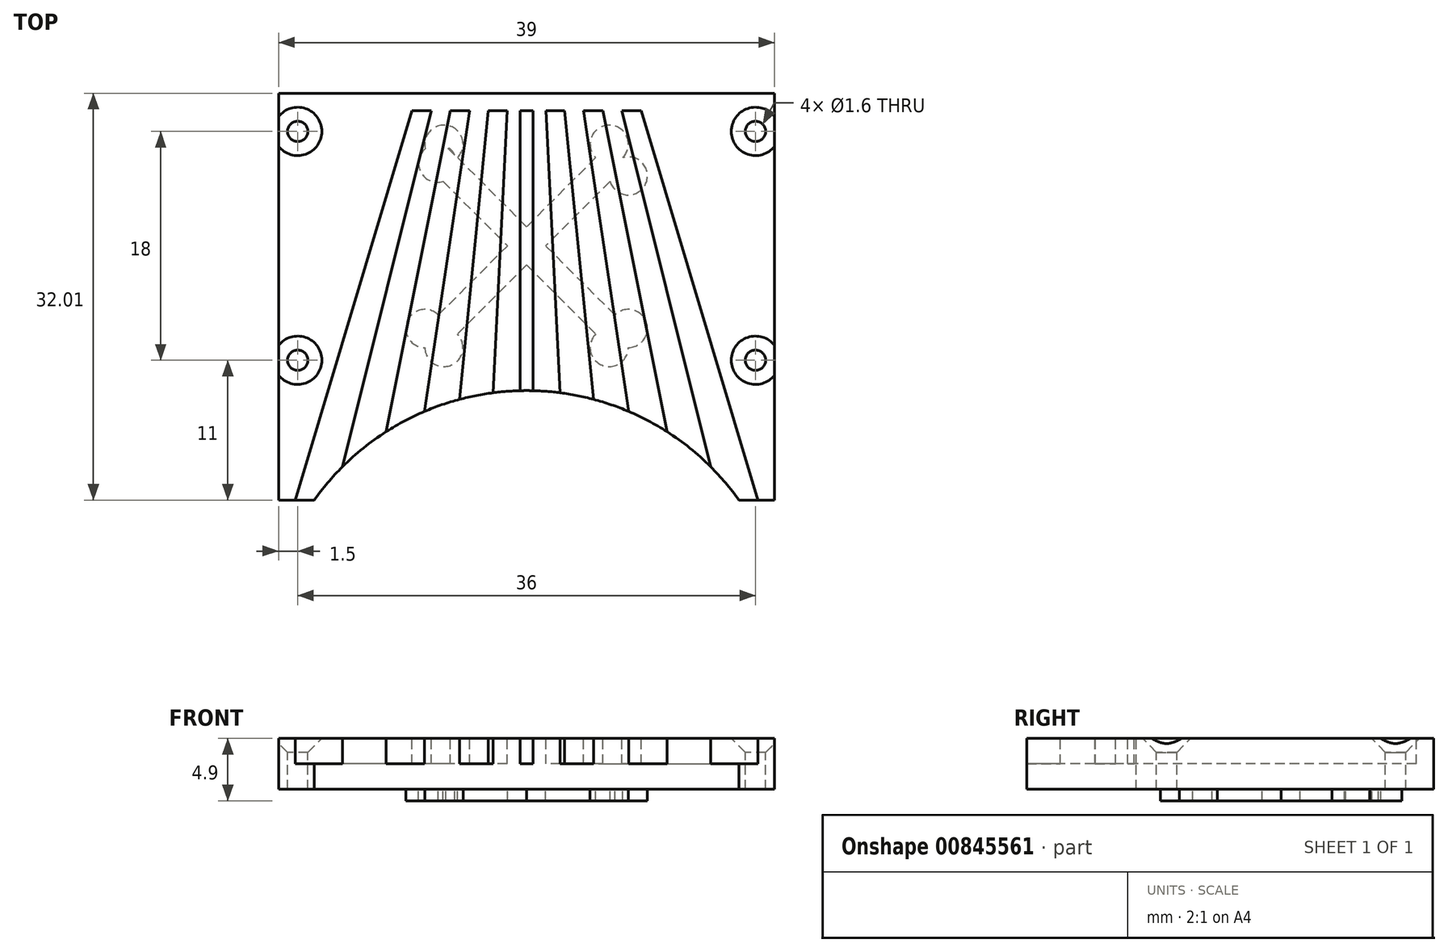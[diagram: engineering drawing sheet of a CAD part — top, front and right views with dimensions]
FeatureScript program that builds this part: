
annotation { "Feature Type Name" : "Feature", "Feature Type Description" : "" }
export const myFeature = defineFeature(function(context is Context, id is Id, definition is map)
    precondition{}
    {
        {
            var Q0;
            Q0=qCreatedBy(makeId("Top.planeOp"),FACE);
            var sketch = newSketch(context, id + "F0", { "sketchPlane" : qUnion([Q0])});
            skLineSegment(sketch, "E0.bottom", {"start": v(19.5, -20) * mm, "end": v(-19.5, -20) * mm});
            skLineSegment(sketch, "E0.top", {"start": v(19.5, 20) * mm, "end": v(-19.5, 20) * mm});
            skLineSegment(sketch, "E0.left", {"start": v(19.5, -20) * mm, "end": v(19.5, 20) * mm});
            skLineSegment(sketch, "E0.right", {"start": v(-19.5, -20) * mm, "end": v(-19.5, 20) * mm});
            skPoint(sketch, "E0.middle", {"position": v(0, 0) * mm});
            skSolve(sketch);
        }
        {
            var Q0;
            Q0=makeQuery(id+"F0.imprint","IMPRINT",FACE,{"disambiguationData":[TD([[makeQuery(id+"F0.imprint","IMPRINT",EDGE,{"derivedFrom":sQuery(id+"F0.wireOp",EDGE,"E0.bottom")}),-1.0]])]});
            extrude(context, id + "F1", {"entities" : qUnion([Q0]), "depth" : 4 * mm});
        }
        {
            var Q0;
            Q0=makeQuery(id+"F1.opExtrude","CAP_FACE",FACE,{"disambiguationData":[OSD([sQuery(id+"F0.wireOp",EDGE,"E0.bottom"),sQuery(id+"F0.wireOp",EDGE,"E0.top"),sQuery(id+"F0.wireOp",EDGE,"E0.left"),sQuery(id+"F0.wireOp",EDGE,"E0.right")])],"isStart":true});
            var sketch = newSketch(context, id + "F2", { "sketchPlane" : qUnion([Q0])});
            skLineSegment(sketch, "E1.bottom", {"start": v(-20.5, 20) * mm, "end": v(20.5, 20) * mm});
            skLineSegment(sketch, "E1.top", {"start": v(-20.5, -12) * mm, "end": v(20.5, -12) * mm});
            skLineSegment(sketch, "E1.left", {"start": v(-20.5, 20) * mm, "end": v(-20.5, -12) * mm});
            skLineSegment(sketch, "E1.right", {"start": v(20.5, 20) * mm, "end": v(20.5, -12) * mm});
            skSolve(sketch);
        }
        {
            var Q0;
            Q0=makeQuery(id+"F1.opExtrude","CAP_FACE",FACE,{"disambiguationData":[OSD([sQuery(id+"F0.wireOp",EDGE,"E0.bottom"),sQuery(id+"F0.wireOp",EDGE,"E0.top"),sQuery(id+"F0.wireOp",EDGE,"E0.left"),sQuery(id+"F0.wireOp",EDGE,"E0.right")])],"isStart":false});
            var sketch = newSketch(context, id + "F3", { "sketchPlane" : qUnion([Q0])});
            skLineSegment(sketch, "E2.left", {"start": v(-20.5, -20) * mm, "end": v(-20.5, 5) * mm});
            skCircle(sketch, "E3", {"center": v(0, -31.89) * mm, "radius": 20.5 * mm});
            skLineSegment(sketch, "E4.left", {"start": v(20.5, -20) * mm, "end": v(20.5, 5) * mm});
            skSolve(sketch);
        }
        {
            var Q0;
            Q0=makeQuery(id+"F3.imprint","IMPRINT",FACE,{"disambiguationData":[TD([[makeQuery(id+"F3.imprint","IMPRINT",EDGE,{"derivedFrom":sQuery(id+"F3.wireOp",EDGE,"E3")}),1.0]])]});
            extrude(context, id + "F4", {"entities" : qUnion([Q0]), "operationType" : NewBodyOperationType.REMOVE, "oppositeDirection" : true, "depth" : 25 * mm});
        }
        {
            var Q0;
            Q0=makeQuery(id+"F1.opExtrude","CAP_FACE",FACE,{"disambiguationData":[OSD([sQuery(id+"F0.wireOp",EDGE,"E0.bottom"),sQuery(id+"F0.wireOp",EDGE,"E0.top"),sQuery(id+"F0.wireOp",EDGE,"E0.left"),sQuery(id+"F0.wireOp",EDGE,"E0.right")])],"isStart":false});
            var sketch = newSketch(context, id + "F5", { "sketchPlane" : qUnion([Q0])});
            skLineSegment(sketch, "E5.bottom", {"start": v(19.5, 20) * mm, "end": v(-19.5, 20) * mm});
            skLineSegment(sketch, "E5.top", {"start": v(19.5, 12) * mm, "end": v(-19.5, 12) * mm});
            skLineSegment(sketch, "E5.left", {"start": v(19.5, 20) * mm, "end": v(19.5, 12) * mm});
            skLineSegment(sketch, "E5.right", {"start": v(-19.5, 20) * mm, "end": v(-19.5, 12) * mm});
            skSolve(sketch);
        }
        {
            var Q0;
            Q0=makeQuery(id+"F5.imprint","IMPRINT",FACE,{"disambiguationData":[TD([[makeQuery(id+"F5.imprint","IMPRINT",EDGE,{"derivedFrom":sQuery(id+"F5.wireOp",EDGE,"E5.bottom")}),1.0]])]});
            extrude(context, id + "F6", {"entities" : qUnion([Q0]), "operationType" : NewBodyOperationType.REMOVE, "oppositeDirection" : true, "depth" : 25 * mm});
        }
        {
            var Q0;
            Q0=makeQuery(id+"F1.opExtrude","CAP_FACE",FACE,{"disambiguationData":[OSD([sQuery(id+"F0.wireOp",EDGE,"E0.bottom"),sQuery(id+"F0.wireOp",EDGE,"E0.top"),sQuery(id+"F0.wireOp",EDGE,"E0.left"),sQuery(id+"F0.wireOp",EDGE,"E0.right")])],"isStart":false});
            var sketch = newSketch(context, id + "F7", { "sketchPlane" : qUnion([Q0])});
            skCircle(sketch, "E6", {"center": v(0, 40.68) * mm, "radius": 20.5 * mm});
            skLineSegment(sketch, "E7", {"start": v(0, 40.68) * mm, "end": v(0, -11.39) * mm, "construction": true});
            skLineSegment(sketch, "E8", {"start": v(0, 40.68) * mm, "end": v(2.51, -8.88) * mm, "construction": true});
            skLineSegment(sketch, "E9", {"start": v(0, 40.68) * mm, "end": v(5.03, -9.7) * mm, "construction": true});
            skLineSegment(sketch, "E10.bottom", {"start": v(-0.5, 10.63) * mm, "end": v(0.5, 10.63) * mm});
            skLineSegment(sketch, "E10.top", {"start": v(-0.5, -16.72) * mm, "end": v(0.5, -16.72) * mm});
            skLineSegment(sketch, "E10.left", {"start": v(-0.5, 10.63) * mm, "end": v(-0.5, -16.72) * mm});
            skLineSegment(sketch, "E10.right", {"start": v(0.5, 10.63) * mm, "end": v(0.5, -16.72) * mm});
            skPoint(sketch, "E10.middle", {"position": v(0, -3.05) * mm});
            skLineSegment(sketch, "E11", {"start": v(0, 40.68) * mm, "end": v(7.5, -9.48) * mm, "construction": true});
            skLineSegment(sketch, "E12", {"start": v(0, 40.68) * mm, "end": v(10.03, -9.53) * mm, "construction": true});
            skLineSegment(sketch, "E13", {"start": v(0, 40.68) * mm, "end": v(12.45, -9.27) * mm, "construction": true});
            skLineSegment(sketch, "E14", {"start": v(0, 40.68) * mm, "end": v(15, -9.32) * mm, "construction": true});
            skLineSegment(sketch, "E15", {"start": v(0, 40.68) * mm, "end": v(-2.53, -9.2) * mm, "construction": true});
            skLineSegment(sketch, "E16", {"start": v(0, 40.68) * mm, "end": v(-4.93, -8.73) * mm, "construction": true});
            skLineSegment(sketch, "E17", {"start": v(0, 40.68) * mm, "end": v(-7.45, -9.16) * mm, "construction": true});
            skLineSegment(sketch, "E18", {"start": v(0, 40.68) * mm, "end": v(-10.25, -10.6) * mm, "construction": true});
            skLineSegment(sketch, "E19", {"start": v(0, 40.68) * mm, "end": v(-12.9, -11.1) * mm, "construction": true});
            skLineSegment(sketch, "E20", {"start": v(0, 40.68) * mm, "end": v(-15.32, -10.37) * mm, "construction": true});
            skLineSegment(sketch, "E21", {"start": v(-0.5, 10.63) * mm, "end": v(-19.5, 10.63) * mm, "construction": true});
            skLineSegment(sketch, "E22", {"start": v(0.5, 10.63) * mm, "end": v(19.5, 10.63) * mm, "construction": true});
            skLineSegment(sketch, "E23", {"start": v(9.02, 10.63) * mm, "end": v(9.52, 10.63) * mm});
            skLineSegment(sketch, "E24", {"start": v(9.02, 10.63) * mm, "end": v(8.52, 10.63) * mm});
            skLineSegment(sketch, "E25", {"start": v(7.5, 10.63) * mm, "end": v(8, 10.63) * mm});
            skLineSegment(sketch, "E26", {"start": v(7.5, 10.63) * mm, "end": v(7, 10.63) * mm});
            skLineSegment(sketch, "E27", {"start": v(6, 10.63) * mm, "end": v(6.5, 10.63) * mm});
            skLineSegment(sketch, "E28", {"start": v(6, 10.63) * mm, "end": v(5.5, 10.63) * mm});
            skLineSegment(sketch, "E29", {"start": v(4.5, 10.63) * mm, "end": v(5, 10.63) * mm});
            skLineSegment(sketch, "E30", {"start": v(4.5, 10.63) * mm, "end": v(3.99, 10.63) * mm});
            skLineSegment(sketch, "E31", {"start": v(3, 10.63) * mm, "end": v(3.5, 10.63) * mm});
            skLineSegment(sketch, "E32", {"start": v(3, 10.63) * mm, "end": v(2.5, 10.63) * mm});
            skLineSegment(sketch, "E33", {"start": v(1.52, 10.63) * mm, "end": v(2.03, 10.63) * mm});
            skLineSegment(sketch, "E34", {"start": v(1.52, 10.63) * mm, "end": v(1.02, 10.63) * mm});
            skLineSegment(sketch, "E35", {"start": v(-1.52, 10.63) * mm, "end": v(-1.02, 10.63) * mm});
            skLineSegment(sketch, "E36", {"start": v(-1.52, 10.63) * mm, "end": v(-2.02, 10.63) * mm});
            skLineSegment(sketch, "E37", {"start": v(-3, 10.63) * mm, "end": v(-2.5, 10.63) * mm});
            skLineSegment(sketch, "E38", {"start": v(-3, 10.63) * mm, "end": v(-3.5, 10.63) * mm});
            skLineSegment(sketch, "E39", {"start": v(-4.5, 10.63) * mm, "end": v(-3.98, 10.63) * mm});
            skLineSegment(sketch, "E40", {"start": v(-4.5, 10.63) * mm, "end": v(-5, 10.63) * mm});
            skLineSegment(sketch, "E41", {"start": v(-6, 10.63) * mm, "end": v(-5.5, 10.63) * mm});
            skLineSegment(sketch, "E42", {"start": v(-6, 10.63) * mm, "end": v(-6.5, 10.63) * mm});
            skLineSegment(sketch, "E43", {"start": v(-7.5, 10.63) * mm, "end": v(-7, 10.63) * mm});
            skLineSegment(sketch, "E44", {"start": v(-7.5, 10.63) * mm, "end": v(-8, 10.63) * mm});
            skLineSegment(sketch, "E45", {"start": v(-9.02, 10.63) * mm, "end": v(-8.5, 10.63) * mm});
            skLineSegment(sketch, "E46", {"start": v(-9.02, 10.63) * mm, "end": v(-9.52, 10.63) * mm});
            skLineSegment(sketch, "E47", {"start": v(19.5, -20) * mm, "end": v(-19.5, -20) * mm, "construction": true});
            skLineSegment(sketch, "E48", {"start": v(18.2, -20) * mm, "end": v(18.7, -20) * mm});
            skLineSegment(sketch, "E49", {"start": v(18.2, -20) * mm, "end": v(17.7, -20) * mm});
            skLineSegment(sketch, "E50", {"start": v(15.13, -20) * mm, "end": v(15.63, -20) * mm});
            skLineSegment(sketch, "E51", {"start": v(15.13, -20) * mm, "end": v(14.63, -20) * mm});
            skLineSegment(sketch, "E52", {"start": v(12.12, -20) * mm, "end": v(12.63, -20) * mm});
            skLineSegment(sketch, "E53", {"start": v(12.12, -20) * mm, "end": v(11.62, -20) * mm});
            skLineSegment(sketch, "E54", {"start": v(9.07, -20) * mm, "end": v(9.57, -20) * mm});
            skLineSegment(sketch, "E55", {"start": v(9.07, -20) * mm, "end": v(8.57, -20) * mm});
            skLineSegment(sketch, "E56", {"start": v(6.06, -20) * mm, "end": v(6.56, -20) * mm});
            skLineSegment(sketch, "E57", {"start": v(6.06, -20) * mm, "end": v(5.56, -20) * mm});
            skLineSegment(sketch, "E58", {"start": v(3.08, -20) * mm, "end": v(3.58, -20) * mm});
            skLineSegment(sketch, "E59", {"start": v(3.08, -20) * mm, "end": v(2.57, -20) * mm});
            skLineSegment(sketch, "E60", {"start": v(-3.07, -20) * mm, "end": v(-2.57, -20) * mm});
            skLineSegment(sketch, "E61", {"start": v(-3.07, -20) * mm, "end": v(-3.57, -20) * mm});
            skLineSegment(sketch, "E62", {"start": v(-6.06, -20) * mm, "end": v(-5.55, -20) * mm});
            skLineSegment(sketch, "E63", {"start": v(-6.06, -20) * mm, "end": v(-6.56, -20) * mm});
            skLineSegment(sketch, "E64", {"start": v(-9.06, -20) * mm, "end": v(-8.56, -20) * mm});
            skLineSegment(sketch, "E65", {"start": v(-9.06, -20) * mm, "end": v(-9.56, -20) * mm});
            skLineSegment(sketch, "E66", {"start": v(-12.12, -20) * mm, "end": v(-11.62, -20) * mm});
            skLineSegment(sketch, "E67", {"start": v(-12.12, -20) * mm, "end": v(-12.63, -20) * mm});
            skLineSegment(sketch, "E68", {"start": v(-15.13, -20) * mm, "end": v(-14.63, -20) * mm});
            skLineSegment(sketch, "E69", {"start": v(-15.13, -20) * mm, "end": v(-15.63, -20) * mm});
            skLineSegment(sketch, "E70", {"start": v(-18.2, -20) * mm, "end": v(-17.7, -20) * mm});
            skLineSegment(sketch, "E71", {"start": v(-18.2, -20) * mm, "end": v(-18.7, -20) * mm});
            skLineSegment(sketch, "E72", {"start": v(1.52, 10.63) * mm, "end": v(3.08, -20) * mm});
            skLineSegment(sketch, "E73", {"start": v(3, 10.63) * mm, "end": v(6.06, -20) * mm});
            skLineSegment(sketch, "E74", {"start": v(4.5, 10.63) * mm, "end": v(9.07, -20) * mm});
            skLineSegment(sketch, "E75", {"start": v(6, 10.63) * mm, "end": v(12.12, -20) * mm});
            skLineSegment(sketch, "E76", {"start": v(7.5, 10.63) * mm, "end": v(15.13, -20) * mm});
            skLineSegment(sketch, "E77", {"start": v(9.02, 10.63) * mm, "end": v(18.2, -20) * mm});
            skLineSegment(sketch, "E78", {"start": v(9.02, 10.63) * mm, "end": v(7.5, 10.63) * mm});
            skLineSegment(sketch, "E79", {"start": v(6, 10.63) * mm, "end": v(4.5, 10.63) * mm});
            skLineSegment(sketch, "E80", {"start": v(3, 10.63) * mm, "end": v(1.52, 10.63) * mm});
            skLineSegment(sketch, "E81", {"start": v(18.2, -20) * mm, "end": v(15.13, -20) * mm});
            skLineSegment(sketch, "E82", {"start": v(12.12, -20) * mm, "end": v(9.07, -20) * mm});
            skLineSegment(sketch, "E83", {"start": v(6.06, -20) * mm, "end": v(3.08, -20) * mm});
            skLineSegment(sketch, "E84", {"start": v(-1.52, 10.63) * mm, "end": v(-3.07, -20) * mm});
            skLineSegment(sketch, "E85", {"start": v(-3, 10.63) * mm, "end": v(-6.06, -20) * mm});
            skLineSegment(sketch, "E86", {"start": v(-4.5, 10.63) * mm, "end": v(-9.06, -20) * mm});
            skLineSegment(sketch, "E87", {"start": v(-6, 10.63) * mm, "end": v(-12.12, -20) * mm});
            skLineSegment(sketch, "E88", {"start": v(-7.5, 10.63) * mm, "end": v(-15.13, -20) * mm});
            skLineSegment(sketch, "E89", {"start": v(-9.02, 10.63) * mm, "end": v(-18.2, -20) * mm});
            skLineSegment(sketch, "E90", {"start": v(-1.52, 10.63) * mm, "end": v(-3, 10.63) * mm});
            skLineSegment(sketch, "E91", {"start": v(-4.5, 10.63) * mm, "end": v(-6, 10.63) * mm});
            skLineSegment(sketch, "E92", {"start": v(-7.5, 10.63) * mm, "end": v(-9.02, 10.63) * mm});
            skLineSegment(sketch, "E93", {"start": v(-3.07, -20) * mm, "end": v(-6.06, -20) * mm});
            skLineSegment(sketch, "E94", {"start": v(-9.06, -20) * mm, "end": v(-12.12, -20) * mm});
            skLineSegment(sketch, "E95", {"start": v(-15.13, -20) * mm, "end": v(-18.2, -20) * mm});
            skSolve(sketch);
        }
        {
            var Q0;
            Q0=makeQuery(id+"F1.opExtrude","CAP_FACE",FACE,{"disambiguationData":[OSD([sQuery(id+"F0.wireOp",EDGE,"E0.bottom"),sQuery(id+"F0.wireOp",EDGE,"E0.top"),sQuery(id+"F0.wireOp",EDGE,"E0.left"),sQuery(id+"F0.wireOp",EDGE,"E0.right")])],"isStart":false});
            var sketch = newSketch(context, id + "F8", { "sketchPlane" : qUnion([Q0])});
            skLineSegment(sketch, "E96.bottom", {"start": v(-18, -9) * mm, "end": v(18, -9) * mm, "construction": true});
            skLineSegment(sketch, "E96.top", {"start": v(-18, 9) * mm, "end": v(18, 9) * mm, "construction": true});
            skLineSegment(sketch, "E96.left", {"start": v(-18, -9) * mm, "end": v(-18, 9) * mm, "construction": true});
            skLineSegment(sketch, "E96.right", {"start": v(18, -9) * mm, "end": v(18, 9) * mm, "construction": true});
            skPoint(sketch, "E96.middle", {"position": v(0, 0) * mm});
            skCircle(sketch, "E97", {"center": v(18, 9) * mm, "radius": 0.8 * mm});
            skCircle(sketch, "E98", {"center": v(18, -9) * mm, "radius": 0.8 * mm});
            skCircle(sketch, "E99", {"center": v(-18, 9) * mm, "radius": 0.8 * mm});
            skCircle(sketch, "E100", {"center": v(-18, -9) * mm, "radius": 0.8 * mm});
            skSolve(sketch);
        }
        {
            var Q0;
            Q0=sQuery(id+"F8.wireOp",VERTEX,"E97.center");
            var Q1;
            Q1=sQuery(id+"F8.wireOp",VERTEX,"E98.center");
            var Q2;
            Q2=sQuery(id+"F8.wireOp",VERTEX,"E99.center");
            var Q3;
            Q3=sQuery(id+"F8.wireOp",VERTEX,"E100.center");
            var Q4;
            Q4=makeQuery(id+"F1.opExtrude","SWEPT_BODY",BODY,{"disambiguationData":[OSD([sQuery(id+"F0.wireOp",EDGE,"E0.bottom"),sQuery(id+"F0.wireOp",EDGE,"E0.top"),sQuery(id+"F0.wireOp",EDGE,"E0.left"),sQuery(id+"F0.wireOp",EDGE,"E0.right")])]});
            hole(context, id + "F9", {"style" : HoleStyle.C_SINK, "endStyle" : HoleEndStyle.THROUGH, "holeDiameter" : 1.6 * mm, "cSinkDiameter" : 3.8 * mm, "cSinkAngle" : 90 * degree, "isTappedThrough" : true, "tappedDepth" : 12 * mm, "tapClearance" : 3, "locations" : qUnion([Q0, Q1, Q2, Q3]), "scope" : qUnion([Q4])});
        }
        {
            var Q0;
            Q0=makeQuery(id+"F7.imprint","IMPRINT",FACE,{"disambiguationData":[TD([[makeQuery(id+"F7.imprint","IMPRINT",EDGE,{"derivedFrom":sQuery(id+"F7.wireOp",EDGE,"E23")}),-1.0]])]});
            var Q1;
            {var subQ5=sQuery(id+"F7.wireOp",EDGE,"E27");Q1=makeQuery(id+"F7.imprint","IMPRINT",FACE,{"disambiguationData":[TD([[makeQuery(id+"F7.imprint","IMPRINT",EDGE,{"derivedFrom":subQ5}),-1.0]])]});}
            var Q2;
            {var subQ5=sQuery(id+"F7.wireOp",EDGE,"E31");Q2=makeQuery(id+"F7.imprint","IMPRINT",FACE,{"disambiguationData":[TD([[makeQuery(id+"F7.imprint","IMPRINT",EDGE,{"derivedFrom":subQ5}),-1.0]])]});}
            var Q3;
            {var subQ0=sQuery(id+"F7.wireOp",EDGE,"E10.bottom");Q3=makeQuery(id+"F7.imprint","IMPRINT",FACE,{"disambiguationData":[TD([[makeQuery(id+"F7.imprint","IMPRINT",EDGE,{"derivedFrom":subQ0}),-1.0]])]});}
            var Q4;
            {var subQ5=sQuery(id+"F7.wireOp",EDGE,"E37");Q4=makeQuery(id+"F7.imprint","IMPRINT",FACE,{"disambiguationData":[TD([[makeQuery(id+"F7.imprint","IMPRINT",EDGE,{"derivedFrom":subQ5}),-1.0]])]});}
            var Q5;
            {var subQ5=sQuery(id+"F7.wireOp",EDGE,"E41");Q5=makeQuery(id+"F7.imprint","IMPRINT",FACE,{"disambiguationData":[TD([[makeQuery(id+"F7.imprint","IMPRINT",EDGE,{"derivedFrom":subQ5}),-1.0]])]});}
            var Q6;
            Q6=makeQuery(id+"F7.imprint","IMPRINT",FACE,{"disambiguationData":[TD([[makeQuery(id+"F7.imprint","IMPRINT",EDGE,{"derivedFrom":sQuery(id+"F7.wireOp",EDGE,"E45")}),-1.0]])]});
            extrude(context, id + "F10", {"entities" : qUnion([Q0, Q1, Q2, Q3, Q4, Q5, Q6]), "operationType" : NewBodyOperationType.REMOVE, "oppositeDirection" : true, "depth" : 2 * mm});
        }
        {
            var Q0;
            Q0=makeQuery(id+"F2.imprint","IMPRINT",FACE,{"disambiguationData":[TD([[makeQuery(id+"F2.imprint","IMPRINT",EDGE,{"derivedFrom":sQuery(id+"F2.wireOp",EDGE,"E1.bottom")}),1.0]])]});
            var sketch = newSketch(context, id + "F11", { "sketchPlane" : qUnion([Q0])});
            skLineSegment(sketch, "E101.bottom", {"start": v(-8, 8) * mm, "end": v(8, 8) * mm, "construction": true});
            skLineSegment(sketch, "E101.top", {"start": v(-8, -8) * mm, "end": v(8, -8) * mm, "construction": true});
            skLineSegment(sketch, "E101.left", {"start": v(-8, 8) * mm, "end": v(-8, -8) * mm, "construction": true});
            skLineSegment(sketch, "E101.right", {"start": v(8, 8) * mm, "end": v(8, -8) * mm, "construction": true});
            skPoint(sketch, "E101.middle", {"position": v(0, 0) * mm});
            skLineSegment(sketch, "E102", {"start": v(8, -8) * mm, "end": v(8, -6.5) * mm, "construction": true});
            skLineSegment(sketch, "E103", {"start": v(8, -8) * mm, "end": v(6.5, -8) * mm, "construction": true});
            skLineSegment(sketch, "E104", {"start": v(8, 8) * mm, "end": v(8, 6.5) * mm, "construction": true});
            skLineSegment(sketch, "E105", {"start": v(8, 8) * mm, "end": v(6.5, 8) * mm, "construction": true});
            skLineSegment(sketch, "E106", {"start": v(-8, 8) * mm, "end": v(-8, 6.5) * mm, "construction": true});
            skLineSegment(sketch, "E107", {"start": v(-8, 8) * mm, "end": v(-6.5, 8) * mm, "construction": true});
            skLineSegment(sketch, "E108", {"start": v(-8, -8) * mm, "end": v(-8, -6.5) * mm, "construction": true});
            skLineSegment(sketch, "E109", {"start": v(-8, -8) * mm, "end": v(-6.5, -8) * mm, "construction": true});
            skLineSegment(sketch, "E110", {"start": v(8, -6.5) * mm, "end": v(8, -5.5) * mm, "construction": true});
            skLineSegment(sketch, "E111", {"start": v(-8, -6.5) * mm, "end": v(-7, -6.5) * mm, "construction": true});
            skLineSegment(sketch, "E112", {"start": v(8, 6.5) * mm, "end": v(-6.5, -8) * mm});
            skLineSegment(sketch, "E113", {"start": v(-8, -6.5) * mm, "end": v(6.5, 8) * mm});
            skLineSegment(sketch, "E114", {"start": v(8, -6.5) * mm, "end": v(-6.5, 8) * mm});
            skLineSegment(sketch, "E115", {"start": v(6.5, -8) * mm, "end": v(-8, 6.5) * mm});
            skCircle(sketch, "E116", {"center": v(8, 6.5) * mm, "radius": 1.5 * mm});
            skCircle(sketch, "E117", {"center": v(6.5, 8) * mm, "radius": 1.5 * mm});
            skCircle(sketch, "E118", {"center": v(-6.5, 8) * mm, "radius": 1.5 * mm});
            skCircle(sketch, "E119", {"center": v(-8, 6.5) * mm, "radius": 1.5 * mm});
            skCircle(sketch, "E120", {"center": v(-6.5, -8) * mm, "radius": 1.5 * mm});
            skCircle(sketch, "E121", {"center": v(6.5, -8) * mm, "radius": 1.5 * mm});
            skCircle(sketch, "E122", {"center": v(8, -5.5) * mm, "radius": 1.5 * mm});
            skCircle(sketch, "E123", {"center": v(-7, -6.5) * mm, "radius": 1.5 * mm});
            skSolve(sketch);
        }
        {
            var Q0;
            Q0=qSketchRegion(id+"F11",true);
            extrude(context, id + "F12", {"entities" : qUnion([Q0]), "operationType" : NewBodyOperationType.ADD, "depth" : 0.9 * mm});
        }
        {
            var Q0;
            {var subQ3=sQuery(id+"F7.wireOp",EDGE,"E77");Q0=makeQuery(id+"F7.imprint","IMPRINT",FACE,{"disambiguationData":[TD([[makeQuery(id+"F7.imprint","IMPRINT",EDGE,{"derivedFrom":subQ3}),-1.0]])]});}
            var Q1;
            {var subQ0=sQuery(id+"F7.wireOp",EDGE,"E79");var subQ1=makeQuery(id+"F7.imprint","IMPRINT",VERTEX,{"disambiguationData":[OD(0.0)],"derivedFrom":subQ0});Q1=makeQuery(id+"F7.imprint","IMPRINT",FACE,{"disambiguationData":[TD([[makeQuery(id+"F7.imprint","IMPRINT",EDGE,{"disambiguationData":[TD([[subQ1,-1.0]])],"derivedFrom":subQ0}),1.0]])]});}
            var Q2;
            {var subQ0=sQuery(id+"F7.wireOp",EDGE,"E80");var subQ1=makeQuery(id+"F7.imprint","IMPRINT",VERTEX,{"disambiguationData":[OD(0.0)],"derivedFrom":subQ0});Q2=makeQuery(id+"F7.imprint","IMPRINT",FACE,{"disambiguationData":[TD([[makeQuery(id+"F7.imprint","IMPRINT",EDGE,{"disambiguationData":[TD([[subQ1,-1.0]])],"derivedFrom":subQ0}),1.0]])]});}
            var Q3;
            {var subQ0=sQuery(id+"F7.wireOp",EDGE,"E10.bottom");Q3=makeQuery(id+"F7.imprint","IMPRINT",FACE,{"disambiguationData":[TD([[makeQuery(id+"F7.imprint","IMPRINT",EDGE,{"derivedFrom":subQ0}),-1.0]])]});}
            var Q4;
            {var subQ0=sQuery(id+"F7.wireOp",EDGE,"E90");var subQ3=makeQuery(id+"F7.imprint","IMPRINT",VERTEX,{"disambiguationData":[OD(0.0)],"derivedFrom":subQ0});Q4=makeQuery(id+"F7.imprint","IMPRINT",FACE,{"disambiguationData":[TD([[makeQuery(id+"F7.imprint","IMPRINT",EDGE,{"disambiguationData":[TD([[subQ3,-1.0]])],"derivedFrom":subQ0}),1.0]])]});}
            var Q5;
            {var subQ0=sQuery(id+"F7.wireOp",EDGE,"E91");var subQ1=makeQuery(id+"F7.imprint","IMPRINT",VERTEX,{"disambiguationData":[OD(0.0)],"derivedFrom":subQ0});Q5=makeQuery(id+"F7.imprint","IMPRINT",FACE,{"disambiguationData":[TD([[makeQuery(id+"F7.imprint","IMPRINT",EDGE,{"disambiguationData":[TD([[subQ1,-1.0]])],"derivedFrom":subQ0}),1.0]])]});}
            var Q6;
            {var subQ4=sQuery(id+"F7.wireOp",EDGE,"E89");Q6=makeQuery(id+"F7.imprint","IMPRINT",FACE,{"disambiguationData":[TD([[makeQuery(id+"F7.imprint","IMPRINT",EDGE,{"derivedFrom":subQ4}),1.0]])]});}
            extrude(context, id + "F13", {"entities" : qUnion([Q0, Q1, Q2, Q3, Q4, Q5, Q6]), "operationType" : NewBodyOperationType.REMOVE, "oppositeDirection" : true, "depth" : 2 * mm});
        }
    });
